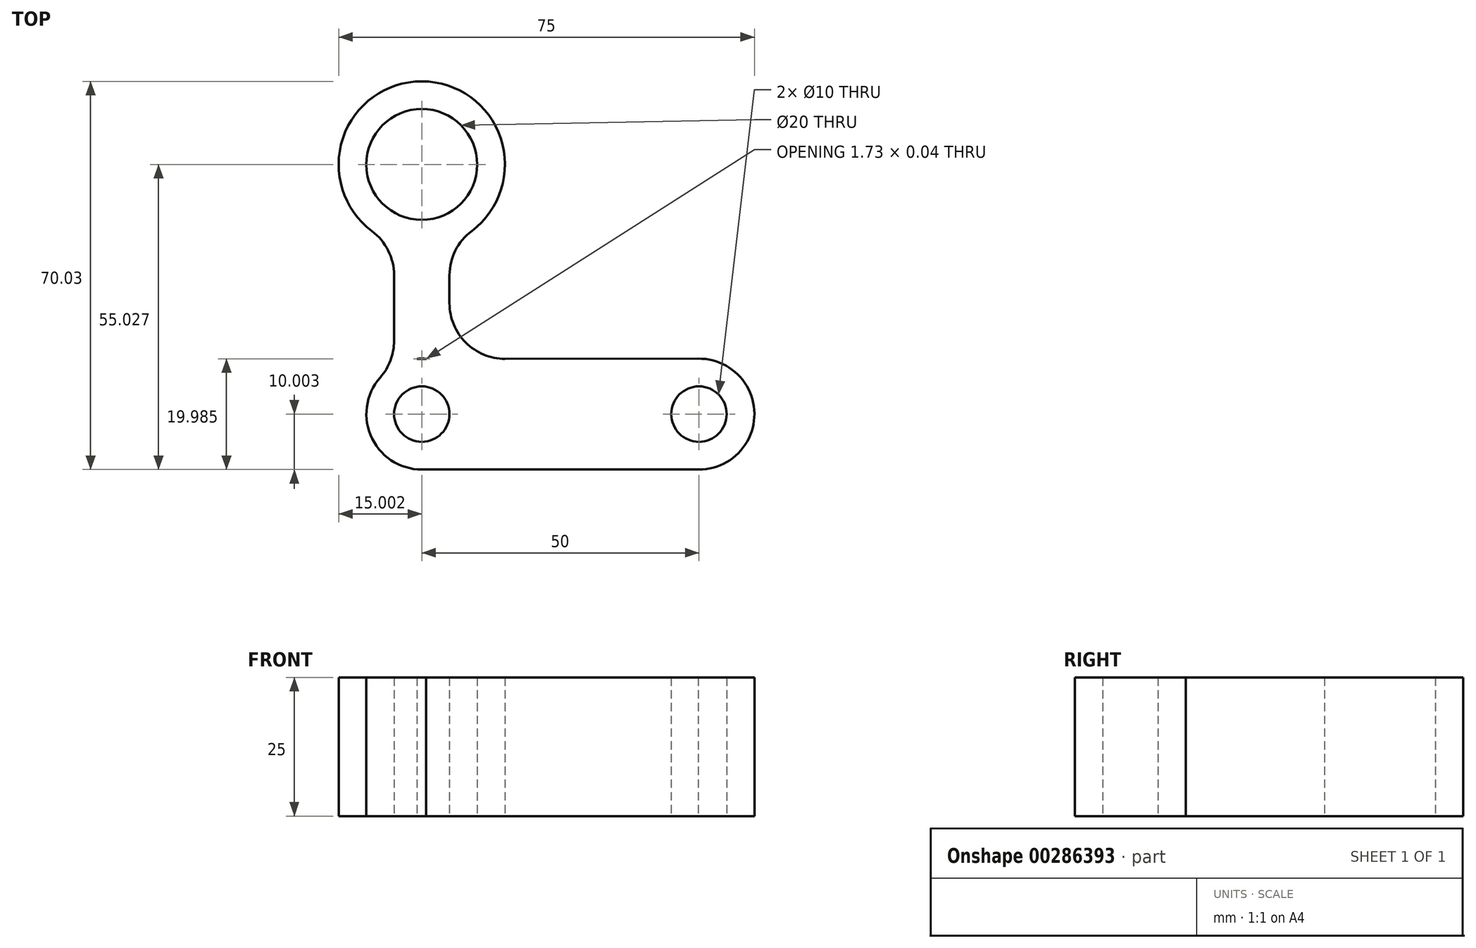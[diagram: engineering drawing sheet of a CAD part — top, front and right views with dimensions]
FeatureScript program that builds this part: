
annotation { "Feature Type Name" : "Feature", "Feature Type Description" : "" }
export const myFeature = defineFeature(function(context is Context, id is Id, definition is map)
    precondition{}
    {
        {
            var Q0;
            Q0=qCreatedBy(makeId("Top.planeOp"),FACE);
            var sketch = newSketch(context, id + "F0", { "sketchPlane" : qUnion([Q0])});
            skArc(sketch, "E0", {"start": v(-13.04, -13.68) * mm, "mid": v(-13.9, -13.65) * mm, "end": v(-14.77, -13.68) * mm});
            skCircle(sketch, "E1", {"center": v(-13.9, -23.65) * mm, "radius": 5 * mm});
            skCircle(sketch, "E2", {"center": v(36.1, -23.65) * mm, "radius": 5 * mm});
            skLineSegment(sketch, "E3", {"start": v(-14.77, -13.68) * mm, "end": v(-13.04, -13.68) * mm});
            skLineSegment(sketch, "E4", {"start": v(-13.9, -23.65) * mm, "end": v(-13.9, -13.65) * mm});
            skArc(sketch, "E5", {"start": v(-4.9, 9.38) * mm, "mid": v(-13.9, 36.38) * mm, "end": v(-22.9, 9.38) * mm});
            skCircle(sketch, "E6", {"center": v(-13.9, 21.38) * mm, "radius": 10 * mm});
            skLineSegment(sketch, "E7", {"start": v(-8.9, 1.38) * mm, "end": v(-8.9, 3.74) * mm});
            skLineSegment(sketch, "E8", {"start": v(-18.9, 1.38) * mm, "end": v(-18.9, -10.42) * mm});
            skLineSegment(sketch, "E9", {"start": v(-8.9, 3.74) * mm, "end": v(-8.9, -3.67) * mm});
            skPoint(sketch, "E10.orphan", {"position": v(-13.9, 3.74) * mm});
            skLineSegment(sketch, "E11", {"start": v(-13.9, 21.38) * mm, "end": v(-13.9, -23.65) * mm, "construction": true});
            skPoint(sketch, "E12.start.orphan", {"position": v(-18.9, 4.83) * mm});
            skPoint(sketch, "E13.start.orphan", {"position": v(-20.62, -31.06) * mm});
            skArc(sketch, "E14", {"start": v(36.09, -33.65) * mm, "mid": v(46.1, -23.57) * mm, "end": v(35.93, -13.65) * mm});
            skLineSegment(sketch, "E15", {"start": v(-13.9, -23.65) * mm, "end": v(36.1, -23.65) * mm});
            skLineSegment(sketch, "E16", {"start": v(-13.15, -33.62) * mm, "end": v(36.09, -33.65) * mm});
            skLineSegment(sketch, "E17", {"start": v(35.93, -13.65) * mm, "end": v(1.1, -13.67) * mm});
            skArc(sketch, "E18.trimOffspring", {"start": v(-21.4, -17.03) * mm, "mid": v(-22.86, -28.1) * mm, "end": v(-13.15, -33.62) * mm});
            skArc(sketch, "E19.filletArc", {"start": v(-8.9, -3.67) * mm, "mid": v(-5.98, -10.75) * mm, "end": v(1.1, -13.67) * mm});
            skPoint(sketch, "E20.visualSharp", {"position": v(-8.9, 7.24) * mm});
            skArc(sketch, "E20.filletArc", {"start": v(-4.9, 9.38) * mm, "mid": v(-7.85, 5.85) * mm, "end": v(-8.9, 1.38) * mm});
            skPoint(sketch, "E21.visualSharp", {"position": v(-18.9, -14.99) * mm});
            skArc(sketch, "E21.filletArc", {"start": v(-21.4, -17.03) * mm, "mid": v(-19.55, -13.95) * mm, "end": v(-18.9, -10.42) * mm});
            skPoint(sketch, "E22.visualSharp", {"position": v(-18.9, 7.24) * mm});
            skArc(sketch, "E22.filletArc", {"start": v(-18.9, 1.38) * mm, "mid": v(-19.96, 5.85) * mm, "end": v(-22.9, 9.38) * mm});
            skSolve(sketch);
        }
        {
            var Q0;
            Q0 = qSketchRegion(id + "F0", true);
            extrude(context, id + "F1", {"entities" : qUnion([Q0]), "depth" : 25 * mm});
        }
    });
